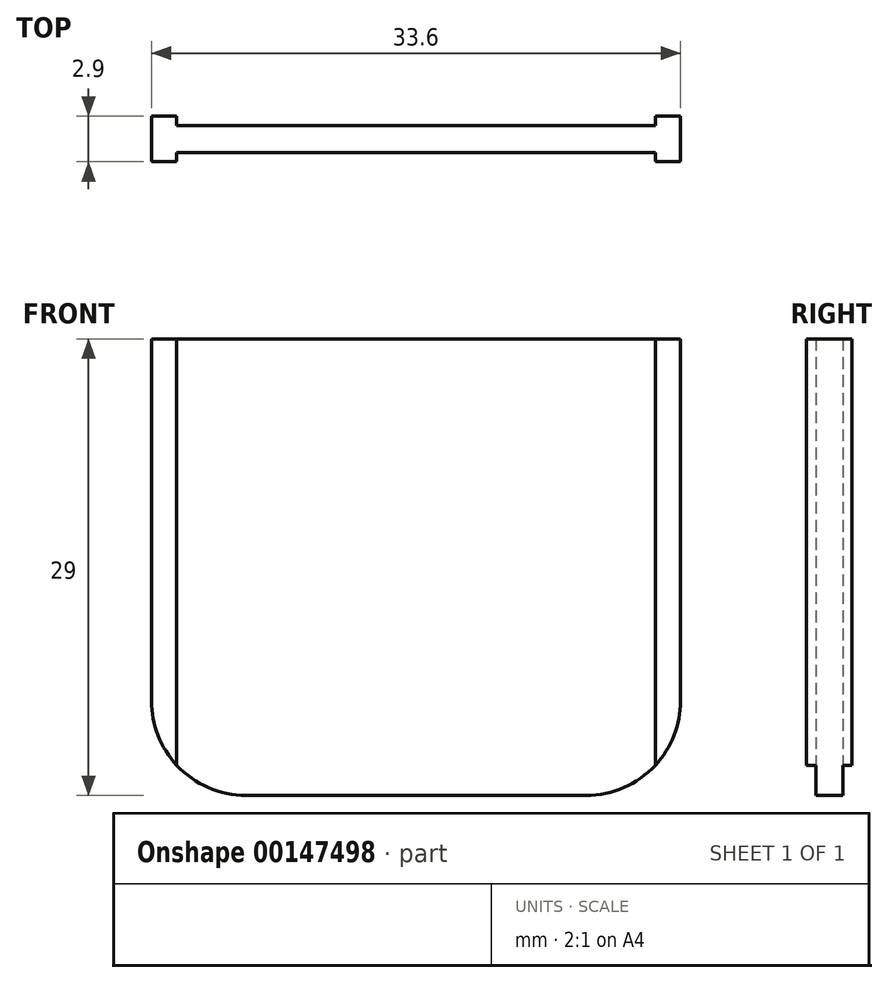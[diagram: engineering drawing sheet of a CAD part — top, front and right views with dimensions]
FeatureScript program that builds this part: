
annotation { "Feature Type Name" : "Feature", "Feature Type Description" : "" }
export const myFeature = defineFeature(function(context is Context, id is Id, definition is map)
    precondition{}
    {
        {
            var Q0;
            Q0=qCreatedBy(makeId("Top.planeOp"),FACE);
            var sketch = newSketch(context, id + "F0", { "sketchPlane" : qUnion([Q0])});
            skLineSegment(sketch, "E0.bottom", {"start": v(-16, 0.86) * mm, "end": v(16, 0.86) * mm});
            skLineSegment(sketch, "E0.top", {"start": v(-16, -0.86) * mm, "end": v(16, -0.86) * mm});
            skLineSegment(sketch, "E0.left", {"start": v(-16, 0.86) * mm, "end": v(-16, -0.86) * mm});
            skLineSegment(sketch, "E0.right", {"start": v(16, 0.86) * mm, "end": v(16, -0.86) * mm});
            skPoint(sketch, "E0.middle", {"position": v(0, 0) * mm});
            skLineSegment(sketch, "E1.bottom", {"start": v(-16.8, 1.44) * mm, "end": v(-15.2, 1.44) * mm});
            skLineSegment(sketch, "E1.top", {"start": v(-16.8, -1.45) * mm, "end": v(-15.2, -1.45) * mm});
            skLineSegment(sketch, "E1.left", {"start": v(-16.8, 1.44) * mm, "end": v(-16.8, -1.45) * mm});
            skLineSegment(sketch, "E1.right", {"start": v(-15.2, 1.44) * mm, "end": v(-15.2, -1.45) * mm});
            skPoint(sketch, "E1.middle", {"position": v(-16, 0) * mm});
            skLineSegment(sketch, "E2.bottom", {"start": v(15.2, 1.45) * mm, "end": v(16.8, 1.45) * mm});
            skLineSegment(sketch, "E2.top", {"start": v(15.2, -1.45) * mm, "end": v(16.8, -1.45) * mm});
            skLineSegment(sketch, "E2.left", {"start": v(15.2, 1.45) * mm, "end": v(15.2, -1.45) * mm});
            skLineSegment(sketch, "E2.right", {"start": v(16.8, 1.45) * mm, "end": v(16.8, -1.45) * mm});
            skPoint(sketch, "E2.middle", {"position": v(16, 0) * mm});
            skSolve(sketch);
        }
        {
            var Q0;
            Q0 = qSketchRegion(id + "F0", true);
            extrude(context, id + "F1", {"entities" : qUnion([Q0]), "depth" : 29 * mm});
        }
        {
            var Q0;
            Q0=makeQuery(id+"F1.opExtrude","CAP_EDGE",EDGE,{"disambiguationData":[OSD([sQuery(id+"F0.wireOp",EDGE,"E1.left")])],"isStart":true});
            var Q1;
            Q1=makeQuery(id+"F1.opExtrude","CAP_EDGE",EDGE,{"disambiguationData":[OSD([sQuery(id+"F0.wireOp",EDGE,"E2.right")])],"isStart":true});
            fillet(context, id + "F2", {"entities" : qUnion([Q0, Q1]), "radius" : 6 * mm, "tangentPropagation" : true, "allowEdgeOverflow" : false});
        }
    });
